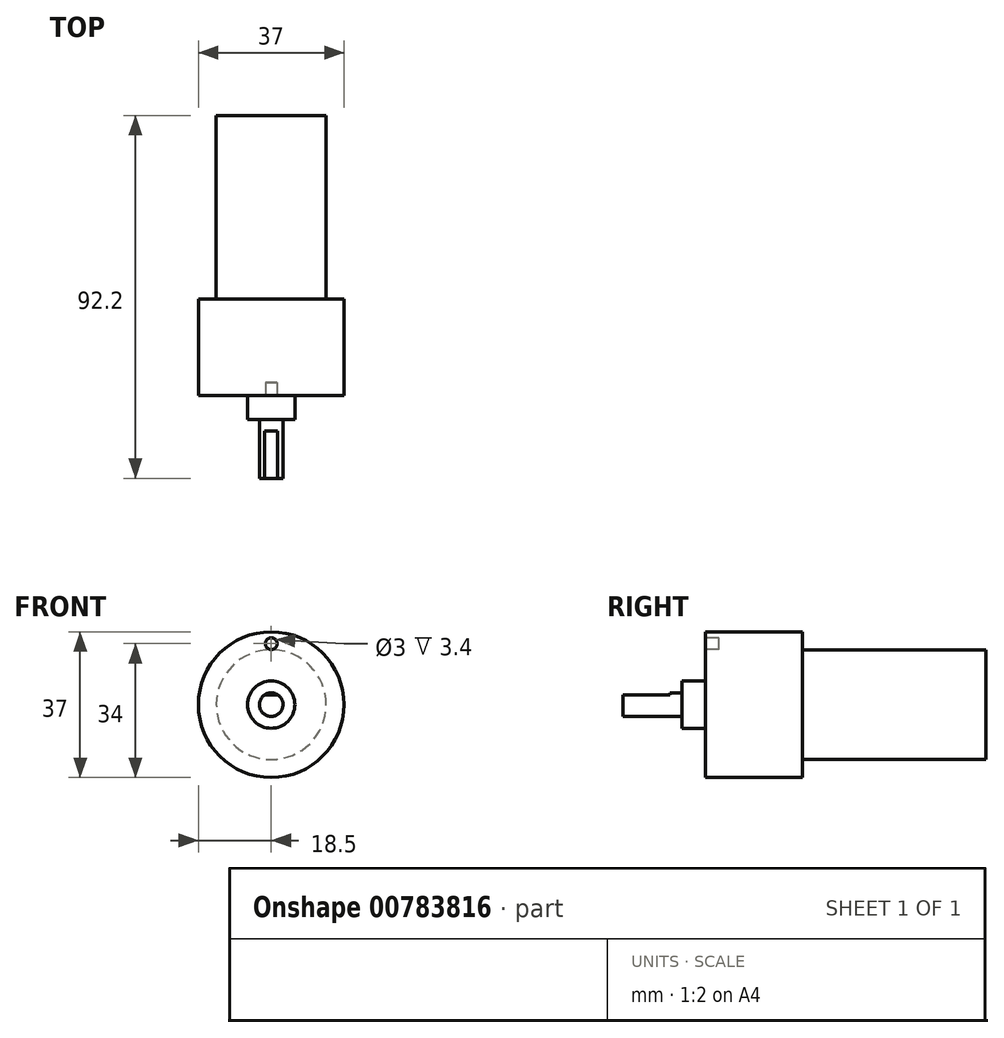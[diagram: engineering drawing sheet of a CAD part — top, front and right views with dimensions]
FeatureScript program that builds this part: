
annotation { "Feature Type Name" : "Feature", "Feature Type Description" : "" }
export const myFeature = defineFeature(function(context is Context, id is Id, definition is map)
    precondition{}
    {
        {
            var Q0;
            Q0=qCreatedBy(makeId("Front.planeOp"),FACE);
            var sketch = newSketch(context, id + "F0", { "sketchPlane" : qUnion([Q0])});
            skCircle(sketch, "E0", {"center": v(0, 0) * mm, "radius": 13.95 * mm});
            skSolve(sketch);
        }
        {
            var Q0;
            Q0=makeQuery(id+"F0.imprint","IMPRINT",FACE,{"disambiguationData":[TD([[makeQuery(id+"F0.imprint","IMPRINT",EDGE,{"derivedFrom":sQuery(id+"F0.wireOp",EDGE,"E0")}),1.0]])]});
            extrude(context, id + "F1", {"entities" : qUnion([Q0]), "depth" : 46.6 * mm, "offsetDistance" : 25 * mm});
        }
        {
            var Q0;
            Q0=makeQuery(id+"F1.opExtrude","CAP_FACE",FACE,{"disambiguationData":[OSD([sQuery(id+"F0.wireOp",EDGE,"E0")])],"isStart":false});
            var sketch = newSketch(context, id + "F2", { "sketchPlane" : qUnion([Q0])});
            skCircle(sketch, "E1", {"center": v(0, 0) * mm, "radius": 18.5 * mm});
            skSolve(sketch);
        }
        {
            var Q0;
            Q0=makeQuery(id+"F2.imprint","IMPRINT",FACE,{"disambiguationData":[TD([[makeQuery(id+"F2.imprint","IMPRINT",EDGE,{"derivedFrom":sQuery(id+"F2.wireOp",EDGE,"E1")}),1.0]])]});
            var Q1;
            Q1=makeQuery(id+"F2.imprint","IMPRINT",FACE,{"disambiguationData":[TD([[makeQuery(id+"F2.imprint","IMPRINT",EDGE,{"derivedFrom":makeQuery(id+"F1.opExtrude","CAP_EDGE",EDGE,{"disambiguationData":[OSD([sQuery(id+"F0.wireOp",EDGE,"E0")])],"isStart":false})}),1.0]])]});
            extrude(context, id + "F3", {"entities" : qUnion([Q0, Q1]), "operationType" : NewBodyOperationType.ADD, "depth" : 24.6 * mm, "offsetDistance" : 25 * mm});
        }
        {
            var Q0;
            Q0=makeQuery(id+"F3.opExtrude","CAP_FACE",FACE,{"disambiguationData":[OSD([sQuery(id+"F2.wireOp",EDGE,"E1")])],"isStart":false});
            var sketch = newSketch(context, id + "F4", { "sketchPlane" : qUnion([Q0])});
            skCircle(sketch, "E2", {"center": v(0, 0) * mm, "radius": 6 * mm});
            skSolve(sketch);
        }
        {
            var Q0;
            Q0=makeQuery(id+"F4.imprint","IMPRINT",FACE,{"disambiguationData":[TD([[makeQuery(id+"F4.imprint","IMPRINT",EDGE,{"derivedFrom":sQuery(id+"F4.wireOp",EDGE,"E2")}),1.0]])]});
            extrude(context, id + "F5", {"entities" : qUnion([Q0]), "operationType" : NewBodyOperationType.ADD, "depth" : 6 * mm, "offsetDistance" : 25 * mm});
        }
        {
            var Q0;
            Q0=makeQuery(id+"F5.opExtrude","CAP_FACE",FACE,{"disambiguationData":[OSD([sQuery(id+"F4.wireOp",EDGE,"E2")])],"isStart":false});
            var sketch = newSketch(context, id + "F6", { "sketchPlane" : qUnion([Q0])});
            skCircle(sketch, "E3", {"center": v(0, 0) * mm, "radius": 3 * mm});
            skSolve(sketch);
        }
        {
            var Q0;
            Q0=makeQuery(id+"F6.imprint","IMPRINT",FACE,{"disambiguationData":[TD([[makeQuery(id+"F6.imprint","IMPRINT",EDGE,{"derivedFrom":sQuery(id+"F6.wireOp",EDGE,"E3")}),1.0]])]});
            extrude(context, id + "F7", {"entities" : qUnion([Q0]), "operationType" : NewBodyOperationType.ADD, "depth" : 15 * mm, "offsetDistance" : 25 * mm});
        }
        {
            var Q0;
            Q0=makeQuery(id+"F7.opExtrude","CAP_FACE",FACE,{"disambiguationData":[OSD([sQuery(id+"F6.wireOp",EDGE,"E3")])],"isStart":false});
            var sketch = newSketch(context, id + "F8", { "sketchPlane" : qUnion([Q0])});
            skLineSegment(sketch, "E4.bottom", {"start": v(-6.23, 2.5) * mm, "end": v(9.4, 2.5) * mm});
            skLineSegment(sketch, "E4.top", {"start": v(-6.23, 8.38) * mm, "end": v(9.4, 8.38) * mm});
            skLineSegment(sketch, "E4.left", {"start": v(-6.23, 2.5) * mm, "end": v(-6.23, 8.38) * mm});
            skLineSegment(sketch, "E4.right", {"start": v(9.4, 2.5) * mm, "end": v(9.4, 8.38) * mm});
            skCircle(sketch, "E5.0", {"center": v(0, 0) * mm, "radius": 3 * mm});
            skLineSegment(sketch, "E6", {"start": v(0, 0) * mm, "end": v(0, -3) * mm});
            skLineSegment(sketch, "E7", {"start": v(0, -3) * mm, "end": v(11.48, -3) * mm});
            skSolve(sketch);
        }
        {
            var Q0;
            Q0=makeQuery(id+"F8.imprint","IMPRINT",FACE,{"disambiguationData":[TD([[makeQuery(id+"F8.imprint","IMPRINT",EDGE,{"derivedFrom":sQuery(id+"F8.wireOp",EDGE,"E4.top")}),-1.0]])]});
            var Q1;
            {var subQ0=sQuery(id+"F8.wireOp",EDGE,"E5.0");var subQ1=sQuery(id+"F8.wireOp",EDGE,"E4.bottom");var subQ2=makeQuery(id+"F8.imprint","INTERSECT",VERTEX,{"disambiguationData":[OD(0.0)],"derivedFrom":[subQ1,subQ0]});Q1=makeQuery(id+"F8.imprint","IMPRINT",FACE,{"disambiguationData":[TD([[makeQuery(id+"F8.imprint","IMPRINT",EDGE,{"disambiguationData":[TD([[subQ2,-1.0]])],"derivedFrom":subQ1}),1.0]])]});}
            extrude(context, id + "F9", {"entities" : qUnion([Q0, Q1]), "operationType" : NewBodyOperationType.REMOVE, "oppositeDirection" : true, "depth" : 12 * mm, "offsetDistance" : 25 * mm});
        }
        {
            var Q0;
            Q0=makeQuery(id+"F3.opExtrude","CAP_FACE",FACE,{"disambiguationData":[OSD([sQuery(id+"F2.wireOp",EDGE,"E1")])],"isStart":false});
            var sketch = newSketch(context, id + "F10", { "sketchPlane" : qUnion([Q0])});
            skCircle(sketch, "E8", {"center": v(0, 15.5) * mm, "radius": 1.5 * mm});
            skSolve(sketch);
        }
        {
            var Q0;
            Q0=makeQuery(id+"F10.imprint","IMPRINT",FACE,{"disambiguationData":[TD([[makeQuery(id+"F10.imprint","IMPRINT",EDGE,{"derivedFrom":sQuery(id+"F10.wireOp",EDGE,"E8")}),1.0]])]});
            extrude(context, id + "F11", {"entities" : qUnion([Q0]), "operationType" : NewBodyOperationType.REMOVE, "oppositeDirection" : true, "depth" : 3.4 * mm, "offsetDistance" : 25 * mm});
        }
    });
